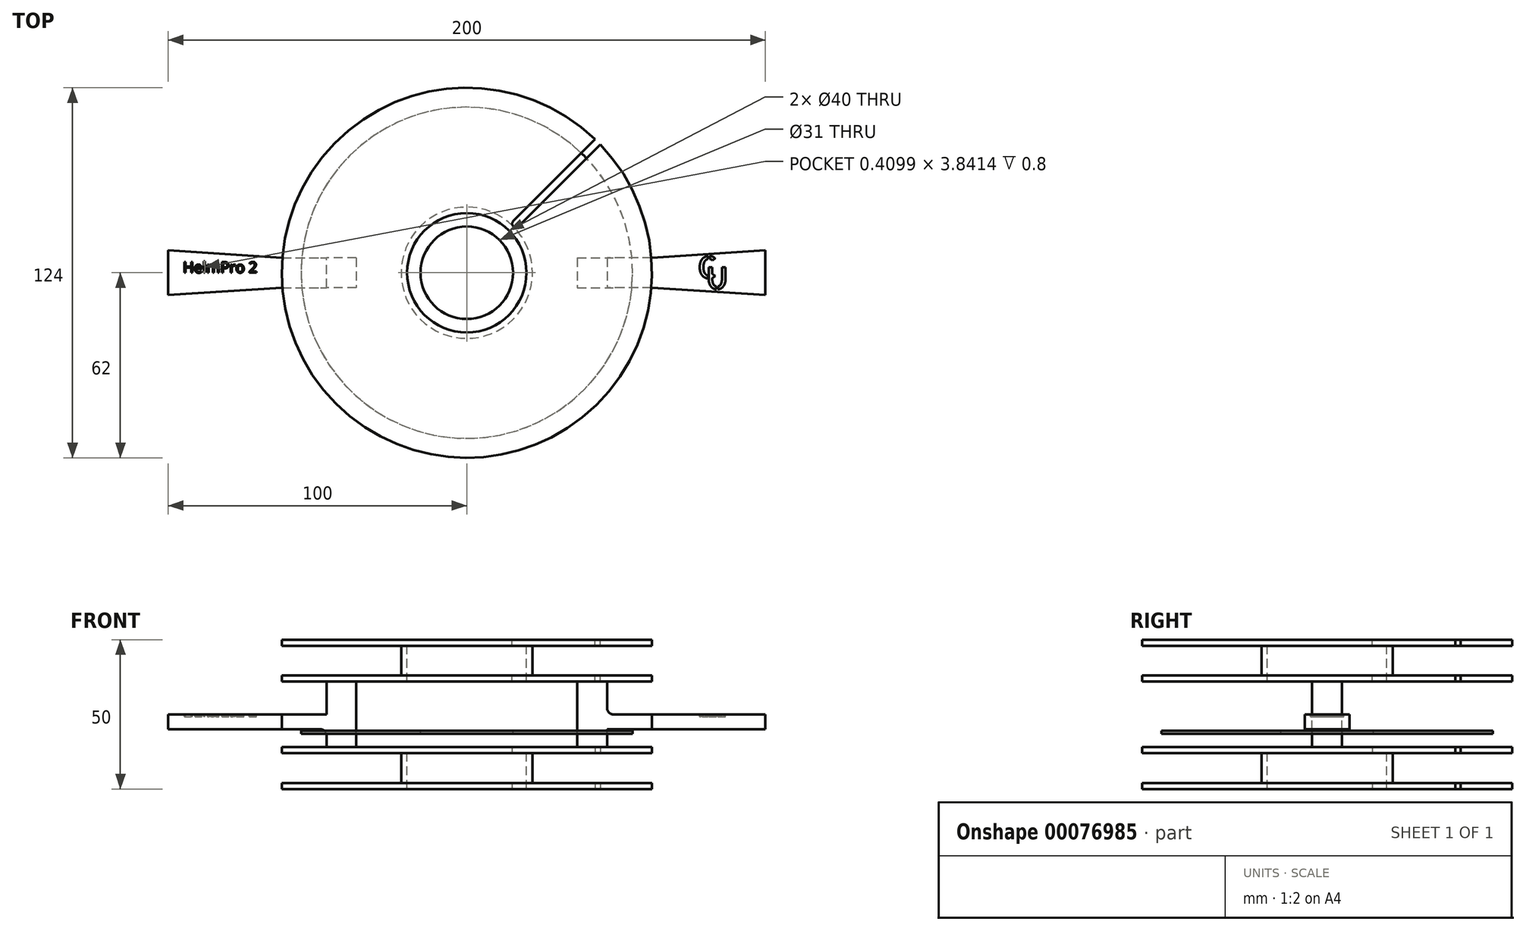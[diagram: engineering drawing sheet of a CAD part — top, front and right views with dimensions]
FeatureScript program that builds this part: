
annotation { "Feature Type Name" : "Feature", "Feature Type Description" : "" }
export const myFeature = defineFeature(function(context is Context, id is Id, definition is map)
    precondition{}
    {
        {
            assignVariable(context, id + "F0", {"name" : "r", "anyValue" : 20});
        }
        {
            assignVariable(context, id + "F1", {"name" : "t", "anyValue" : 2});
        }
        {
            assignVariable(context, id + "F2", {"name" : "h", "anyValue" : 40});
        }
        {
            assignVariable(context, id + "F3", {"name" : "halfLength", "anyValue" : 100});
        }
        {
            assignVariable(context, id + "F4", {"name" : "conWidth", "anyValue" : 10});
        }
        {
            var Q0;
            Q0=qCreatedBy(makeId("Front.planeOp"),FACE);
            var sketch = newSketch(context, id + "F5", { "sketchPlane" : qUnion([Q0])});
            skLineSegment(sketch, "E0", {"start": v(-84.21, 0) * mm, "end": v(84.56, 0) * mm, "construction": true});
            skLineSegment(sketch, "E1", {"start": v(0, 84.95) * mm, "end": v(0, -84.67) * mm, "construction": true});
            skLineSegment(sketch, "E2.bottom", {"start": v(-62, 25) * mm, "end": v(-20, 25) * mm});
            skLineSegment(sketch, "E2.top", {"start": v(-62, 11) * mm, "end": v(-20, 11) * mm});
            skLineSegment(sketch, "E2.left", {"start": v(-62, 25) * mm, "end": v(-62, 23) * mm});
            skLineSegment(sketch, "E2.right", {"start": v(-20, 25) * mm, "end": v(-20, 11) * mm});
            skLineSegment(sketch, "E3.bottom", {"start": v(-62, 23) * mm, "end": v(-22, 23) * mm});
            skLineSegment(sketch, "E3.top", {"start": v(-62, 13) * mm, "end": v(-22, 13) * mm});
            skLineSegment(sketch, "E3.right", {"start": v(-22, 23) * mm, "end": v(-22, 13) * mm});
            skLineSegment(sketch, "E4.trimOffspring", {"start": v(-62, 13) * mm, "end": v(-62, 11) * mm});
            skLineSegment(sketch, "E5", {"start": v(-41.58, 18) * mm, "end": v(43.85, 18) * mm, "construction": true});
            skPoint(sketch, "E5.startSnap0", {"position": v(-22, 18) * mm});
            skLineSegment(sketch, "E6.MirrorCS", {"start": v(-62, -25) * mm, "end": v(-62, -23) * mm});
            skLineSegment(sketch, "E7.MirrorCS", {"start": v(-62, -13) * mm, "end": v(-62, -11) * mm});
            skLineSegment(sketch, "E8.MirrorCS", {"start": v(-22, -23) * mm, "end": v(-22, -13) * mm});
            skPoint(sketch, "E9.MirrorP", {"position": v(-22, -18) * mm});
            skLineSegment(sketch, "E10.MirrorCS", {"start": v(-20, -25) * mm, "end": v(-20, -11) * mm});
            skLineSegment(sketch, "E11.MirrorCS", {"start": v(-62, -11) * mm, "end": v(-20, -11) * mm});
            skLineSegment(sketch, "E12.MirrorCS", {"start": v(-62, -23) * mm, "end": v(-22, -23) * mm});
            skLineSegment(sketch, "E13.MirrorCS", {"start": v(-62, -13) * mm, "end": v(-22, -13) * mm});
            skLineSegment(sketch, "E14.MirrorCS", {"start": v(-62, -25) * mm, "end": v(-20, -25) * mm});
            skSolve(sketch);
        }
        {
            var Q0;
            Q0=makeQuery(id+"F5.imprint","IMPRINT",FACE,{"disambiguationData":[TD([[makeQuery(id+"F5.imprint","IMPRINT",EDGE,{"derivedFrom":sQuery(id+"F5.wireOp",EDGE,"E2.bottom")}),-1.0]])]});
            var Q1;
            Q1=makeQuery(id+"F5.imprint","IMPRINT",FACE,{"disambiguationData":[TD([[makeQuery(id+"F5.imprint","IMPRINT",EDGE,{"derivedFrom":sQuery(id+"F5.wireOp",EDGE,"E6.MirrorCS")}),-1.0]])]});
            var Q2;
            Q2=sQuery(id+"F5.wireOp",EDGE,"E1");
            revolve(context, id + "F6", {"entities" : qUnion([Q0, Q1]), "axis" : qUnion([Q2]), "revolveType" : RevolveType.FULL});
        }
        {
            var Q0;
            Q0=makeQuery(id+"F6.opRevolve","SWEPT_FACE",FACE,{"disambiguationData":[OSD([sQuery(id+"F5.wireOp",EDGE,"E2.top")])]});
            var sketch = newSketch(context, id + "F7", { "sketchPlane" : qUnion([Q0])});
            skLineSegment(sketch, "E15.rect.bottom", {"start": v(-37, -5) * mm, "end": v(-47, -5) * mm});
            skLineSegment(sketch, "E15.rect.top", {"start": v(-37, 5) * mm, "end": v(-47, 5) * mm});
            skLineSegment(sketch, "E15.rect.left", {"start": v(-37, -5) * mm, "end": v(-37, 5) * mm});
            skLineSegment(sketch, "E15.rect.right", {"start": v(-47, -5) * mm, "end": v(-47, 5) * mm});
            skPoint(sketch, "E15.rect.middle", {"position": v(-42, 0) * mm});
            skLineSegment(sketch, "E16", {"start": v(0, 20) * mm, "end": v(0, -20) * mm, "construction": true});
            skPoint(sketch, "E17.MirrorP", {"position": v(42, 0) * mm});
            skLineSegment(sketch, "E18.MirrorCS", {"start": v(37, -5) * mm, "end": v(47, -5) * mm});
            skLineSegment(sketch, "E19.MirrorCS", {"start": v(37, 5) * mm, "end": v(47, 5) * mm});
            skLineSegment(sketch, "E20.MirrorCS", {"start": v(37, -5) * mm, "end": v(37, 5) * mm});
            skLineSegment(sketch, "E21.MirrorCS", {"start": v(47, -5) * mm, "end": v(47, 5) * mm});
            skSolve(sketch);
        }
        {
            var Q0;
            Q0=makeQuery(id+"F7.imprint","IMPRINT",FACE,{"disambiguationData":[TD([[makeQuery(id+"F7.imprint","IMPRINT",EDGE,{"derivedFrom":sQuery(id+"F7.wireOp",EDGE,"E15.rect.bottom")}),-1.0]])]});
            var Q1;
            Q1=makeQuery(id+"F7.imprint","IMPRINT",FACE,{"disambiguationData":[TD([[makeQuery(id+"F7.imprint","IMPRINT",EDGE,{"derivedFrom":sQuery(id+"F7.wireOp",EDGE,"E18.MirrorCS")}),1.0]])]});
            var Q2;
            Q2=makeQuery(id+"F6.opRevolve","SWEPT_FACE",FACE,{"disambiguationData":[OSD([sQuery(id+"F5.wireOp",EDGE,"E11.MirrorCS")])]});
            extrude(context, id + "F8", {"entities" : qUnion([Q0, Q1]), "endBound" : BoundingType.UP_TO_SURFACE, "endBoundEntityFace" : qUnion([Q2]), "depth" : 25 * mm});
        }
        {
            var Q0;
            Q0=qCreatedBy(makeId("Front.planeOp"),FACE);
            var sketch = newSketch(context, id + "F9", { "sketchPlane" : qUnion([Q0])});
            skLineSegment(sketch, "E22.bottom", {"start": v(-55.5, -5.5) * mm, "end": v(-15.5, -5.5) * mm});
            skLineSegment(sketch, "E22.top", {"start": v(-55.5, -6.5) * mm, "end": v(-15.5, -6.5) * mm});
            skLineSegment(sketch, "E22.left", {"start": v(-55.5, -5.5) * mm, "end": v(-55.5, -6.5) * mm});
            skLineSegment(sketch, "E22.right", {"start": v(-15.5, -5.5) * mm, "end": v(-15.5, -6.5) * mm});
            skSolve(sketch);
        }
        {
            var Q0;
            Q0=makeQuery(id+"F9.imprint","IMPRINT",FACE,{"disambiguationData":[TD([[makeQuery(id+"F9.imprint","IMPRINT",EDGE,{"derivedFrom":sQuery(id+"F9.wireOp",EDGE,"E22.bottom")}),-1.0]])]});
            var Q1;
            Q1=sQuery(id+"F5.wireOp",EDGE,"E1");
            revolve(context, id + "F10", {"entities" : qUnion([Q0]), "axis" : qUnion([Q1]), "revolveType" : RevolveType.FULL});
        }
        {
            var Q0;
            Q0=makeQuery(id+"F6.opRevolve","SWEPT_BODY",BODY,{"disambiguationData":[OSD([sQuery(id+"F5.wireOp",EDGE,"E2.bottom"),sQuery(id+"F5.wireOp",EDGE,"E2.top"),sQuery(id+"F5.wireOp",EDGE,"E2.left"),sQuery(id+"F5.wireOp",EDGE,"E2.right"),sQuery(id+"F5.wireOp",EDGE,"E3.bottom"),sQuery(id+"F5.wireOp",EDGE,"E3.top"),sQuery(id+"F5.wireOp",EDGE,"E3.right"),sQuery(id+"F5.wireOp",EDGE,"E4.trimOffspring")])]});
            var Q1;
            Q1=makeQuery(id+"F10.opRevolve","SWEPT_BODY",BODY,{"disambiguationData":[OSD([sQuery(id+"F9.wireOp",EDGE,"E22.bottom"),sQuery(id+"F9.wireOp",EDGE,"E22.top"),sQuery(id+"F9.wireOp",EDGE,"E22.left"),sQuery(id+"F9.wireOp",EDGE,"E22.right")])]});
            var Q2;
            Q2=makeQuery(id+"FYP3mX2uemgJS03_2.opExtrude","SWEPT_BODY",BODY,{"disambiguationData":[OSD([sQuery(id+"FXE0XL3MbIBWzza_2.wireOp",EDGE,"a7d44569-cf2f-4bde-a008-229d11aa6f8e")])]});
            var Q3;
            Q3=makeQuery(id+"FYP3mX2uemgJS03_2.opExtrude","SWEPT_BODY",BODY,{"disambiguationData":[OSD([sQuery(id+"FXE0XL3MbIBWzza_2.wireOp",EDGE,"d1c8bf16-b973-456d-9911-92ba49ddbda90.MirrorC")])]});
            booleanBodies(context, id + "F11", {"operationType" : BooleanOperationType.UNION, "tools" : qUnion([Q0, Q1, Q2, Q3])});
        }
        {
            var Q0;
            Q0=makeQuery(id+"F11.opBoolean","SPLIT",FACE,{"disambiguationData":[TD([makeQuery(id+"F6.opRevolve","SWEPT_FACE",FACE,{"disambiguationData":[OSD([sQuery(id+"F5.wireOp",EDGE,"E2.top")])]})])],"derivedFrom":makeQuery(id+"F8.opExtrude","SWEPT_FACE",FACE,{"disambiguationData":[OSD([sQuery(id+"F7.wireOp",EDGE,"E21.MirrorCS")])]})});
            var sketch = newSketch(context, id + "F12", { "sketchPlane" : qUnion([Q0])});
            skLineSegment(sketch, "E23.rect.bottom", {"start": v(5, -5) * mm, "end": v(-5, -5) * mm});
            skLineSegment(sketch, "E23.rect.top", {"start": v(5, 0) * mm, "end": v(-5, 0) * mm});
            skLineSegment(sketch, "E23.rect.left", {"start": v(5, -5) * mm, "end": v(5, 0) * mm});
            skLineSegment(sketch, "E23.rect.right", {"start": v(-5, -5) * mm, "end": v(-5, 0) * mm});
            skPoint(sketch, "E23.rect.middle", {"position": v(0, -2.5) * mm});
            skSolve(sketch);
        }
        {
            var Q0;
            Q0=makeQuery(id+"F11.opBoolean","SPLIT",FACE,{"disambiguationData":[TD([makeQuery(id+"F6.opRevolve","SWEPT_FACE",FACE,{"disambiguationData":[OSD([sQuery(id+"F5.wireOp",EDGE,"E2.top")])]})])],"derivedFrom":makeQuery(id+"F8.opExtrude","SWEPT_FACE",FACE,{"disambiguationData":[OSD([sQuery(id+"F7.wireOp",EDGE,"E15.rect.right")])]})});
            var sketch = newSketch(context, id + "F13", { "sketchPlane" : qUnion([Q0])});
            skLineSegment(sketch, "E24.rect.bottom", {"start": v(5, -5) * mm, "end": v(-5, -5) * mm});
            skLineSegment(sketch, "E24.rect.top", {"start": v(5, 0) * mm, "end": v(-5, 0) * mm});
            skLineSegment(sketch, "E24.rect.left", {"start": v(5, -5) * mm, "end": v(5, 0) * mm});
            skLineSegment(sketch, "E24.rect.right", {"start": v(-5, -5) * mm, "end": v(-5, 0) * mm});
            skPoint(sketch, "E24.rect.middle", {"position": v(0, -2.5) * mm});
            skSolve(sketch);
        }
        {
            var Q0;
            Q0=makeQuery(id+"F12.imprint","IMPRINT",FACE,{"disambiguationData":[TD([[makeQuery(id+"F12.imprint","IMPRINT",EDGE,{"derivedFrom":sQuery(id+"F12.wireOp",EDGE,"E23.rect.bottom")}),-1.0]])]});
            extrude(context, id + "F14", {"entities" : qUnion([Q0]), "operationType" : NewBodyOperationType.ADD, "depth" : (getVariable(context, 'halfLength') - getVariable(context, 'r') - getVariable(context, 't') / 2 - getVariable(context, 'h')) * mm});
        }
        {
            var Q0;
            Q0=makeQuery(id+"F13.imprint","IMPRINT",FACE,{"disambiguationData":[TD([[makeQuery(id+"F13.imprint","IMPRINT",EDGE,{"derivedFrom":sQuery(id+"F13.wireOp",EDGE,"E24.rect.bottom")}),-1.0]])]});
            extrude(context, id + "F15", {"entities" : qUnion([Q0]), "operationType" : NewBodyOperationType.ADD, "depth" : (getVariable(context, 'halfLength') - getVariable(context, 'r') - getVariable(context, 't') / 2 - getVariable(context, 'h')) * mm});
        }
        {
            var Q0;
            Q0=makeQuery(id+"F15.opExtrude","SWEPT_FACE",FACE,{"disambiguationData":[OSD([sQuery(id+"F13.wireOp",EDGE,"E24.rect.top")])]});
            var sketch = newSketch(context, id + "F16", { "sketchPlane" : qUnion([Q0])});
            skLineSegment(sketch, "E25", {"start": v(0, 74.99) * mm, "end": v(0, -75.28) * mm, "construction": true});
            skLineSegment(sketch, "E26", {"start": v(123.05, 0) * mm, "end": v(-123.05, 0) * mm, "construction": true});
            skLineSegment(sketch, "E27", {"start": v(-62, 0) * mm, "end": v(-62, 5) * mm});
            skLineSegment(sketch, "E28", {"start": v(-62, 0) * mm, "end": v(-62, -5) * mm});
            skLineSegment(sketch, "E29", {"start": v(-100, 0) * mm, "end": v(-100, 7.5) * mm});
            skLineSegment(sketch, "E30", {"start": v(-100, 0) * mm, "end": v(-100, -7.5) * mm});
            skLineSegment(sketch, "E31", {"start": v(-100, -7.5) * mm, "end": v(-62, -5) * mm});
            skLineSegment(sketch, "E32", {"start": v(-62, 5) * mm, "end": v(-100, 7.5) * mm});
            skLineSegment(sketch, "E33.MirrorCS", {"start": v(62, 0) * mm, "end": v(62, -5) * mm});
            skLineSegment(sketch, "E34.MirrorCS", {"start": v(62, 0) * mm, "end": v(62, 5) * mm});
            skLineSegment(sketch, "E35.MirrorCS", {"start": v(100, 0) * mm, "end": v(100, -7.5) * mm});
            skLineSegment(sketch, "E36.MirrorCS", {"start": v(100, 0) * mm, "end": v(100, 7.5) * mm});
            skLineSegment(sketch, "E37.MirrorCS", {"start": v(100, -7.5) * mm, "end": v(62, -5) * mm});
            skLineSegment(sketch, "E38.MirrorCS", {"start": v(62, 5) * mm, "end": v(100, 7.5) * mm});
            skSolve(sketch);
        }
        {
            var Q0;
            {var subQ3=sQuery(id+"F16.wireOp",EDGE,"E31");Q0=makeQuery(id+"F16.imprint","IMPRINT",FACE,{"disambiguationData":[TD([[makeQuery(id+"F16.imprint","IMPRINT",EDGE,{"derivedFrom":subQ3}),1.0]])]});}
            var Q1;
            {var subQ8=sQuery(id+"F16.wireOp",EDGE,"E27");Q1=makeQuery(id+"F16.imprint","IMPRINT",FACE,{"disambiguationData":[TD([[makeQuery(id+"F16.imprint","IMPRINT",EDGE,{"derivedFrom":subQ8}),1.0]])]});}
            var Q2;
            {var subQ3=sQuery(id+"F16.wireOp",EDGE,"E32");Q2=makeQuery(id+"F16.imprint","IMPRINT",FACE,{"disambiguationData":[TD([[makeQuery(id+"F16.imprint","IMPRINT",EDGE,{"derivedFrom":subQ3}),1.0]])]});}
            var Q3;
            Q3=makeQuery(id+"F16.imprint","IMPRINT",FACE,{"disambiguationData":[TD([[makeQuery(id+"F16.imprint","IMPRINT",EDGE,{"derivedFrom":sQuery(id+"F16.wireOp",EDGE,"E33.MirrorCS")}),1.0]])]});
            extrude(context, id + "F17", {"entities" : qUnion([Q0, Q1, Q2, Q3]), "operationType" : NewBodyOperationType.ADD, "oppositeDirection" : true, "depth" : (getVariable(context, 'conWidth') / 2) * mm});
        }
        {
            var Q0;
            Q0=makeQuery(id+"F14.opExtrude","CAP_EDGE",EDGE,{"disambiguationData":[OSD([sQuery(id+"F12.wireOp",EDGE,"E23.rect.bottom")])],"isStart":true});
            var Q1;
            Q1=makeQuery(id+"F15.opExtrude","CAP_EDGE",EDGE,{"disambiguationData":[OSD([sQuery(id+"F13.wireOp",EDGE,"E24.rect.bottom")])],"isStart":true});
            var Q2;
            Q2=makeQuery(id+"F15.opExtrude","CAP_EDGE",EDGE,{"disambiguationData":[OSD([sQuery(id+"F13.wireOp",EDGE,"E24.rect.top")])],"isStart":true});
            var Q3;
            Q3=makeQuery(id+"F14.opExtrude","CAP_EDGE",EDGE,{"disambiguationData":[OSD([sQuery(id+"F12.wireOp",EDGE,"E23.rect.top")])],"isStart":true});
            fillet(context, id + "F18", {"entities" : qUnion([Q0, Q1, Q2, Q3]), "radius" : (getVariable(context, 't')) * mm, "tangentPropagation" : true, "allowEdgeOverflow" : false});
        }
        {
            var Q0;
            Q0=makeQuery(id+"F6.opRevolve","SWEPT_FACE",FACE,{"disambiguationData":[OSD([sQuery(id+"F5.wireOp",EDGE,"E2.bottom")])]});
            var sketch = newSketch(context, id + "F19", { "sketchPlane" : qUnion([Q0])});
            skLineSegment(sketch, "E39", {"start": v(0, 56.2) * mm, "end": v(0, -68.77) * mm, "construction": true});
            skLineSegment(sketch, "E40", {"start": v(69.6, 0) * mm, "end": v(-69.33, 0) * mm, "construction": true});
            skLineSegment(sketch, "E41", {"start": v(0, 0) * mm, "end": v(67.77, 67.77) * mm, "construction": true});
            skLineSegment(sketch, "E42", {"start": v(15.56, 15.56) * mm, "end": v(15.56, 15.56) * mm});
            skLineSegment(sketch, "E43", {"start": v(17.32, 15.56) * mm, "end": v(44.72, 42.96) * mm});
            skLineSegment(sketch, "E44", {"start": v(44.72, 42.96) * mm, "end": v(42.96, 44.72) * mm});
            skLineSegment(sketch, "E45", {"start": v(42.96, 44.72) * mm, "end": v(15.56, 17.32) * mm});
            skPoint(sketch, "E46.visualSharp", {"position": v(14.67, 16.44) * mm});
            skArc(sketch, "E46.filletArc", {"start": v(15.56, 17.32) * mm, "mid": v(15.2, 16.44) * mm, "end": v(15.56, 15.56) * mm});
            skPoint(sketch, "E47.visualSharp", {"position": v(16.44, 14.67) * mm});
            skArc(sketch, "E47.filletArc", {"start": v(15.56, 15.56) * mm, "mid": v(16.44, 15.2) * mm, "end": v(17.32, 15.56) * mm});
            skSolve(sketch);
        }
        {
            var Q0;
            Q0=makeQuery(id+"F6.opRevolve","SWEPT_FACE",FACE,{"disambiguationData":[OSD([sQuery(id+"F5.wireOp",EDGE,"E14.MirrorCS")])]});
            var sketch = newSketch(context, id + "F20", { "sketchPlane" : qUnion([Q0])});
            skLineSegment(sketch, "E48", {"start": v(0, 0) * mm, "end": v(67.77, -67.77) * mm, "construction": true});
            skLineSegment(sketch, "E49", {"start": v(15.56, -15.56) * mm, "end": v(15.56, -15.56) * mm});
            skLineSegment(sketch, "E50", {"start": v(15.56, -17.32) * mm, "end": v(42.96, -44.72) * mm});
            skLineSegment(sketch, "E51", {"start": v(42.96, -44.72) * mm, "end": v(44.72, -42.96) * mm});
            skLineSegment(sketch, "E52", {"start": v(44.72, -42.96) * mm, "end": v(17.32, -15.56) * mm});
            skPoint(sketch, "E53.visualSharp", {"position": v(16.44, -14.67) * mm});
            skArc(sketch, "E53.filletArc", {"start": v(17.32, -15.56) * mm, "mid": v(16.44, -15.2) * mm, "end": v(15.56, -15.56) * mm});
            skPoint(sketch, "E54.visualSharp", {"position": v(14.67, -16.44) * mm});
            skArc(sketch, "E54.filletArc", {"start": v(15.56, -15.56) * mm, "mid": v(15.2, -16.44) * mm, "end": v(15.56, -17.32) * mm});
            skLineSegment(sketch, "E55", {"start": v(0, 62) * mm, "end": v(0, -62) * mm, "construction": true});
            skLineSegment(sketch, "E56", {"start": v(62, 0) * mm, "end": v(-62, 0) * mm, "construction": true});
            skSolve(sketch);
        }
        {
            var Q0;
            {var subQ1=sQuery(id+"F19.wireOp",EDGE,"E46.filletArc");Q0=makeQuery(id+"F19.imprint","IMPRINT",FACE,{"disambiguationData":[TD([[makeQuery(id+"F19.imprint","IMPRINT",EDGE,{"derivedFrom":subQ1}),1.0]])]});}
            var Q1;
            Q1=makeQuery(id+"F6.opRevolve","SWEPT_FACE",FACE,{"disambiguationData":[OSD([sQuery(id+"F5.wireOp",EDGE,"E2.top")])]});
            extrude(context, id + "F21", {"entities" : qUnion([Q0]), "operationType" : NewBodyOperationType.REMOVE, "endBound" : BoundingType.UP_TO_SURFACE, "oppositeDirection" : true, "endBoundEntityFace" : qUnion([Q1]), "depth" : 25 * mm});
        }
        {
            var Q0;
            {var subQ1=sQuery(id+"F20.wireOp",EDGE,"E53.filletArc");Q0=makeQuery(id+"F20.imprint","IMPRINT",FACE,{"disambiguationData":[TD([[makeQuery(id+"F20.imprint","IMPRINT",EDGE,{"derivedFrom":subQ1}),1.0]])]});}
            var Q1;
            Q1=makeQuery(id+"F6.opRevolve","SWEPT_FACE",FACE,{"disambiguationData":[OSD([sQuery(id+"F5.wireOp",EDGE,"E11.MirrorCS")])]});
            extrude(context, id + "F22", {"entities" : qUnion([Q0]), "operationType" : NewBodyOperationType.REMOVE, "endBound" : BoundingType.UP_TO_SURFACE, "oppositeDirection" : true, "endBoundEntityFace" : qUnion([Q1]), "depth" : 25 * mm});
        }
        {
            var Q0;
            Q0=makeQuery(id+"F17.boolean.opBoolean","MERGE",FACE,{"derivedFrom":[makeQuery(id+"F15.opExtrude","SWEPT_FACE",FACE,{"disambiguationData":[OSD([sQuery(id+"F13.wireOp",EDGE,"E24.rect.top")])]}),makeQuery(id+"F17.opExtrude","CAP_FACE",FACE,{"disambiguationData":[OSD([sQuery(id+"F16.wireOp",EDGE,"E27"),sQuery(id+"F16.wireOp",EDGE,"E28"),sQuery(id+"F16.wireOp",EDGE,"E29"),sQuery(id+"F16.wireOp",EDGE,"E30"),sQuery(id+"F16.wireOp",EDGE,"E31"),sQuery(id+"F16.wireOp",EDGE,"E32")])],"isStart":true})]});
            var sketch = newSketch(context, id + "F23", { "sketchPlane" : qUnion([Q0])});
            skLineSegment(sketch, "E57", {"start": v(-95.11, 1.18) * mm, "end": v(-95.11, 6.11) * mm, "construction": true});
            skText(sketch, "E58", { "text": "HelmPro 2\n", "fontName": "OpenSans-Regular.ttf"});
            const initialGuessF23  = {"E58": [-0.09511, 0, 1, 0, 0.00364]};
            skSetInitialGuess(sketch, initialGuessF23);
            skSolve(sketch);
        }
        {
            var Q0;
            Q0=qSketchRegion(id+"F23",true);
            extrude(context, id + "F24", {"entities" : qUnion([Q0]), "operationType" : NewBodyOperationType.REMOVE, "oppositeDirection" : true, "depth" : .8 * mm});
        }
        {
            var Q0;
            Q0=makeQuery(id+"F17.boolean.opBoolean","MERGE",FACE,{"derivedFrom":[makeQuery(id+"F14.opExtrude","SWEPT_FACE",FACE,{"disambiguationData":[OSD([sQuery(id+"F12.wireOp",EDGE,"E23.rect.top")])]}),makeQuery(id+"F17.opExtrude","CAP_FACE",FACE,{"disambiguationData":[OSD([sQuery(id+"F16.wireOp",EDGE,"E33.MirrorCS"),sQuery(id+"F16.wireOp",EDGE,"E34.MirrorCS"),sQuery(id+"F16.wireOp",EDGE,"E35.MirrorCS"),sQuery(id+"F16.wireOp",EDGE,"E36.MirrorCS"),sQuery(id+"F16.wireOp",EDGE,"E37.MirrorCS"),sQuery(id+"F16.wireOp",EDGE,"E38.MirrorCS")])],"isStart":true})]});
            var sketch = newSketch(context, id + "F25", { "sketchPlane" : qUnion([Q0])});
            skText(sketch, "E59", { "text": "C", "fontName": "AllertaStencil-Regular.ttf"});
            skText(sketch, "E60", { "text": "U", "fontName": "AllertaStencil-Regular.ttf"});
            const initialGuessF25  = {"E59": [0.07722, -0.00188, 1, 0, 0.0074], "E60": [0.08018, -0.0055, 1, 0, 0.00731]};
            skSetInitialGuess(sketch, initialGuessF25);
            skSolve(sketch);
        }
        {
            var Q0;
            Q0=qSketchRegion(id+"F25",true);
            extrude(context, id + "F26", {"entities" : qUnion([Q0]), "operationType" : NewBodyOperationType.REMOVE, "oppositeDirection" : true, "depth" : .8 * mm});
        }
    });
